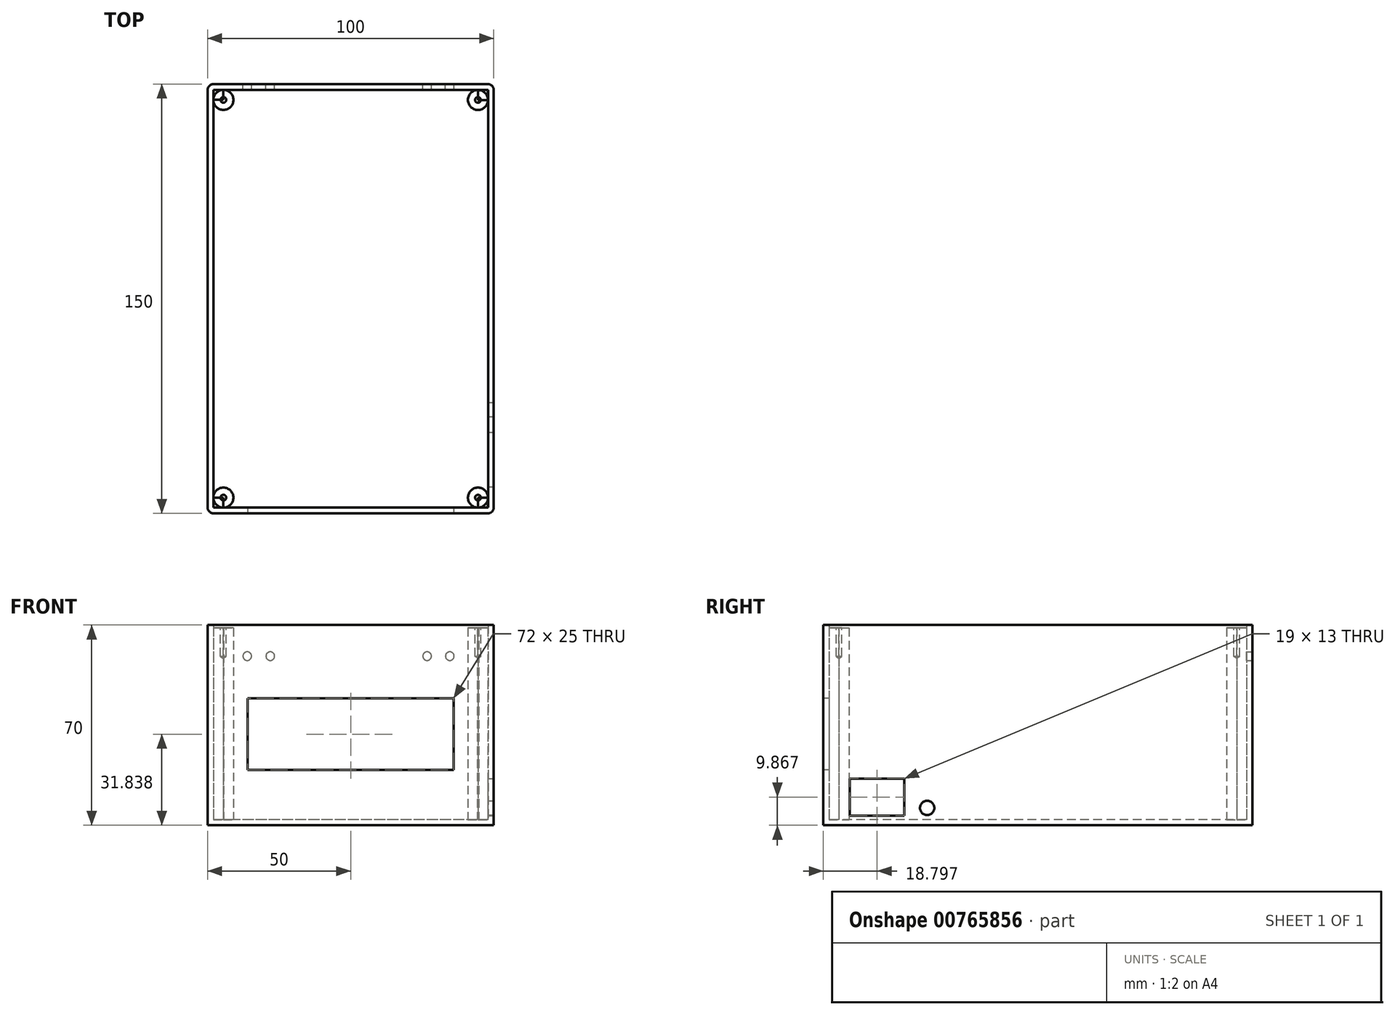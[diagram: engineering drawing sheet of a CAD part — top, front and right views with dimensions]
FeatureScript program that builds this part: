
annotation { "Feature Type Name" : "Feature", "Feature Type Description" : "" }
export const myFeature = defineFeature(function(context is Context, id is Id, definition is map)
    precondition{}
    {
        {
            var Q0;
            Q0=qCreatedBy(makeId("Top.planeOp"),FACE);
            var sketch = newSketch(context, id + "F0", { "sketchPlane" : qUnion([Q0])});
            skLineSegment(sketch, "E0.bottom", {"start": v(50, 75) * mm, "end": v(-50, 75) * mm});
            skLineSegment(sketch, "E0.top", {"start": v(50, -75) * mm, "end": v(-50, -75) * mm});
            skLineSegment(sketch, "E0.left", {"start": v(50, 75) * mm, "end": v(50, -75) * mm});
            skLineSegment(sketch, "E0.right", {"start": v(-50, 75) * mm, "end": v(-50, -75) * mm});
            skPoint(sketch, "E0.middle", {"position": v(0, 0) * mm});
            skSolve(sketch);
        }
        {
            var Q0;
            Q0=qSketchRegion(id+"F0",true);
            extrude(context, id + "F1", {"entities" : qUnion([Q0]), "depth" : 70 * mm, "offsetDistance" : 25.4 * mm});
        }
        {
            var Q0;
            Q0=makeQuery(id+"F1.opExtrude","CAP_FACE",FACE,{"disambiguationData":[OSD([sQuery(id+"F0.wireOp",EDGE,"E0.bottom"),sQuery(id+"F0.wireOp",EDGE,"E0.top"),sQuery(id+"F0.wireOp",EDGE,"E0.left"),sQuery(id+"F0.wireOp",EDGE,"E0.right")])],"isStart":false});
            shell(context, id + "F2", {"entities" : qUnion([Q0]), "thickness" : 2 * mm});
        }
        {
            var Q0;
            Q0=makeQuery(id+"F1.opExtrude","SWEPT_FACE",FACE,{"disambiguationData":[OSD([sQuery(id+"F0.wireOp",EDGE,"E0.top")])]});
            var sketch = newSketch(context, id + "F3", { "sketchPlane" : qUnion([Q0])});
            skLineSegment(sketch, "E1.bottom", {"start": v(-36, 44.34) * mm, "end": v(36, 44.34) * mm});
            skLineSegment(sketch, "E1.top", {"start": v(-36, 19.34) * mm, "end": v(36, 19.34) * mm});
            skLineSegment(sketch, "E1.left", {"start": v(-36, 44.34) * mm, "end": v(-36, 19.34) * mm});
            skLineSegment(sketch, "E1.right", {"start": v(36, 44.34) * mm, "end": v(36, 19.34) * mm});
            skPoint(sketch, "E1.middle", {"position": v(0, 31.84) * mm});
            skSolve(sketch);
        }
        {
            var Q0;
            Q0=qSketchRegion(id+"F3",true);
            extrude(context, id + "F4", {"entities" : qUnion([Q0]), "operationType" : NewBodyOperationType.REMOVE, "oppositeDirection" : true, "depth" : 3 * mm, "offsetDistance" : 25.4 * mm});
        }
        {
            var Q0;
            Q0=makeQuery(id+"F1.opExtrude","SWEPT_FACE",FACE,{"disambiguationData":[OSD([sQuery(id+"F0.wireOp",EDGE,"E0.bottom")])]});
            var sketch = newSketch(context, id + "F5", { "sketchPlane" : qUnion([Q0])});
            skPoint(sketch, "E2", {"position": v(-34.63, 59.1) * mm});
            skPoint(sketch, "E3", {"position": v(-26.71, 59.1) * mm});
            skPoint(sketch, "E4", {"position": v(36.15, 59.1) * mm});
            skPoint(sketch, "E5", {"position": v(28.12, 59.1) * mm});
            skSolve(sketch);
        }
        {
            var Q0;
            Q0=sQuery(id+"F5.wireOp",VERTEX,"E2");
            var Q1;
            Q1=sQuery(id+"F5.wireOp",VERTEX,"E3");
            var Q2;
            Q2=sQuery(id+"F5.wireOp",VERTEX,"E5");
            var Q3;
            Q3=sQuery(id+"F5.wireOp",VERTEX,"E4");
            var Q4;
            Q4=makeQuery(id+"F1.opExtrude","SWEPT_BODY",BODY,{"disambiguationData":[OSD([sQuery(id+"F0.wireOp",EDGE,"E0.bottom"),sQuery(id+"F0.wireOp",EDGE,"E0.top"),sQuery(id+"F0.wireOp",EDGE,"E0.left"),sQuery(id+"F0.wireOp",EDGE,"E0.right")])]});
            hole(context, id + "F6", {"style" : HoleStyle.SIMPLE, "endStyle" : HoleEndStyle.BLIND, "holeDiameter" : 3 * mm, "majorDiameter" : 6.35 * mm, "holeDepth" : 4 * mm, "isTappedThrough" : true, "tappedDepth" : 12.7 * mm, "tapClearance" : 3, "startFromSketch" : true, "locations" : qUnion([Q0, Q1, Q2, Q3]), "scope" : qUnion([Q4])});
        }
        {
            var Q0;
            Q0=makeQuery(id+"F1.opExtrude","SWEPT_FACE",FACE,{"disambiguationData":[OSD([sQuery(id+"F0.wireOp",EDGE,"E0.left")])]});
            var sketch = newSketch(context, id + "F7", { "sketchPlane" : qUnion([Q0])});
            skPoint(sketch, "E6", {"position": v(-38.7, 6.06) * mm});
            skSolve(sketch);
        }
        {
            var Q0;
            Q0=sQuery(id+"F7.wireOp",VERTEX,"E6");
            var Q1;
            Q1=makeQuery(id+"F1.opExtrude","SWEPT_BODY",BODY,{"disambiguationData":[OSD([sQuery(id+"F0.wireOp",EDGE,"E0.bottom"),sQuery(id+"F0.wireOp",EDGE,"E0.top"),sQuery(id+"F0.wireOp",EDGE,"E0.left"),sQuery(id+"F0.wireOp",EDGE,"E0.right")])]});
            hole(context, id + "F8", {"style" : HoleStyle.SIMPLE, "endStyle" : HoleEndStyle.BLIND, "holeDiameter" : 5 * mm, "majorDiameter" : 6.35 * mm, "holeDepth" : 4 * mm, "isTappedThrough" : true, "tappedDepth" : 12.7 * mm, "tapClearance" : 3, "startFromSketch" : true, "locations" : qUnion([Q0]), "scope" : qUnion([Q1])});
        }
        {
            var Q0;
            Q0=makeQuery(id+"F1.opExtrude","SWEPT_EDGE",EDGE,{"disambiguationData":[OSD([sQuery(id+"F0.wireOp",EDGE,"E0.top"),sQuery(id+"F0.wireOp",EDGE,"E0.right")])]});
            var Q1;
            Q1=makeQuery(id+"F1.opExtrude","SWEPT_EDGE",EDGE,{"disambiguationData":[OSD([sQuery(id+"F0.wireOp",EDGE,"E0.bottom"),sQuery(id+"F0.wireOp",EDGE,"E0.right")])]});
            var Q2;
            Q2=makeQuery(id+"F1.opExtrude","SWEPT_EDGE",EDGE,{"disambiguationData":[OSD([sQuery(id+"F0.wireOp",EDGE,"E0.bottom"),sQuery(id+"F0.wireOp",EDGE,"E0.left")])]});
            var Q3;
            Q3=makeQuery(id+"F1.opExtrude","SWEPT_EDGE",EDGE,{"disambiguationData":[OSD([sQuery(id+"F0.wireOp",EDGE,"E0.top"),sQuery(id+"F0.wireOp",EDGE,"E0.left")])]});
            fillet(context, id + "F9", {"entities" : qUnion([Q0, Q1, Q2, Q3]), "radius" : 2 * mm, "tangentPropagation" : true, "allowEdgeOverflow" : false});
        }
        {
            var Q0;
            Q0=makeQuery(id+"F2.opShell","OFFSET_FACE",FACE,{"disambiguationData":[OSD([sQuery(id+"F0.wireOp",EDGE,"E0.bottom"),sQuery(id+"F0.wireOp",EDGE,"E0.top"),sQuery(id+"F0.wireOp",EDGE,"E0.left"),sQuery(id+"F0.wireOp",EDGE,"E0.right")])]});
            var sketch = newSketch(context, id + "F10", { "sketchPlane" : qUnion([Q0])});
            skCircle(sketch, "E7", {"center": v(-44.5, 69.5) * mm, "radius": 3.5 * mm});
            skSolve(sketch);
        }
        {
            var Q0;
            Q0=makeQuery(id+"F10.imprint","IMPRINT",FACE,{"disambiguationData":[TD([[makeQuery(id+"F10.imprint","IMPRINT",EDGE,{"derivedFrom":sQuery(id+"F10.wireOp",EDGE,"E7")}),-1.0]])]});
            var sketch = newSketch(context, id + "F11", { "sketchPlane" : qUnion([Q0])});
            skCircle(sketch, "E8", {"center": v(44.49, 69.47) * mm, "radius": 3.5 * mm});
            skSolve(sketch);
        }
        {
            var Q0;
            Q0=makeQuery(id+"F10.imprint","IMPRINT",FACE,{"disambiguationData":[TD([[makeQuery(id+"F10.imprint","IMPRINT",EDGE,{"derivedFrom":sQuery(id+"F10.wireOp",EDGE,"E7")}),-1.0]])]});
            var sketch = newSketch(context, id + "F12", { "sketchPlane" : qUnion([Q0])});
            skCircle(sketch, "E9", {"center": v(44.5, -69.5) * mm, "radius": 3.5 * mm});
            skSolve(sketch);
        }
        {
            var Q0;
            Q0=makeQuery(id+"F10.imprint","IMPRINT",FACE,{"disambiguationData":[TD([[makeQuery(id+"F10.imprint","IMPRINT",EDGE,{"derivedFrom":sQuery(id+"F10.wireOp",EDGE,"E7")}),-1.0]])]});
            var sketch = newSketch(context, id + "F13", { "sketchPlane" : qUnion([Q0])});
            skCircle(sketch, "E10", {"center": v(-44.5, -69.5) * mm, "radius": 3.5 * mm});
            skSolve(sketch);
        }
        {
            var Q0;
            Q0=qSketchRegion(id+"F10",true);
            var Q1;
            Q1=qSketchRegion(id+"F11",true);
            var Q2;
            Q2=qSketchRegion(id+"F13",true);
            var Q3;
            Q3=qSketchRegion(id+"F12",true);
            extrude(context, id + "F14", {"entities" : qUnion([Q0, Q1, Q2, Q3]), "operationType" : NewBodyOperationType.ADD, "depth" : 67 * mm, "offsetDistance" : 25.4 * mm});
        }
        {
            var Q0;
            Q0=makeQuery(id+"F2.opShell","OFFSET_FACE",FACE,{"disambiguationData":[OSD([sQuery(id+"F0.wireOp",EDGE,"E0.bottom"),sQuery(id+"F0.wireOp",EDGE,"E0.top"),sQuery(id+"F0.wireOp",EDGE,"E0.left"),sQuery(id+"F0.wireOp",EDGE,"E0.right")])]});
            var sketch = newSketch(context, id + "F15", { "sketchPlane" : qUnion([Q0])});
            skLineSegment(sketch, "E11.bottom", {"start": v(-44.5, 69.5) * mm, "end": v(-48, 69.5) * mm});
            skLineSegment(sketch, "E11.top", {"start": v(-44.5, 73) * mm, "end": v(-48, 73) * mm});
            skLineSegment(sketch, "E11.left", {"start": v(-44.5, 69.5) * mm, "end": v(-44.5, 73) * mm});
            skLineSegment(sketch, "E11.right", {"start": v(-48, 69.5) * mm, "end": v(-48, 73) * mm});
            skLineSegment(sketch, "E12.bottom", {"start": v(44.49, 69.47) * mm, "end": v(47.99, 69.47) * mm});
            skLineSegment(sketch, "E12.top", {"start": v(44.49, 72.97) * mm, "end": v(47.99, 72.97) * mm});
            skLineSegment(sketch, "E12.left", {"start": v(44.49, 69.47) * mm, "end": v(44.49, 72.97) * mm});
            skLineSegment(sketch, "E12.right", {"start": v(47.99, 69.47) * mm, "end": v(47.99, 72.97) * mm});
            skLineSegment(sketch, "E13.bottom", {"start": v(44.5, -69.5) * mm, "end": v(48, -69.5) * mm});
            skLineSegment(sketch, "E13.top", {"start": v(44.5, -73) * mm, "end": v(48, -73) * mm});
            skLineSegment(sketch, "E13.left", {"start": v(44.5, -69.5) * mm, "end": v(44.5, -73) * mm});
            skLineSegment(sketch, "E13.right", {"start": v(48, -69.5) * mm, "end": v(48, -73) * mm});
            skLineSegment(sketch, "E14.bottom", {"start": v(-44.5, -69.5) * mm, "end": v(-48, -69.5) * mm});
            skLineSegment(sketch, "E14.top", {"start": v(-44.5, -73) * mm, "end": v(-48, -73) * mm});
            skLineSegment(sketch, "E14.left", {"start": v(-44.5, -69.5) * mm, "end": v(-44.5, -73) * mm});
            skLineSegment(sketch, "E14.right", {"start": v(-48, -69.5) * mm, "end": v(-48, -73) * mm});
            skSolve(sketch);
        }
        {
            var Q0;
            Q0=qSketchRegion(id+"F15",true);
            extrude(context, id + "F16", {"entities" : qUnion([Q0]), "depth" : 67 * mm, "offsetDistance" : 25.4 * mm});
        }
        {
            var Q0;
            Q0=makeQuery(id+"F14.opExtrude","CAP_FACE",FACE,{"disambiguationData":[OSD([sQuery(id+"F10.wireOp",EDGE,"E7")])],"isStart":false});
            var sketch = newSketch(context, id + "F17", { "sketchPlane" : qUnion([Q0])});
            skPoint(sketch, "E15", {"position": v(-44.5, -69.5) * mm});
            skSolve(sketch);
        }
        {
            var Q0;
            Q0=makeQuery(id+"F16.opExtrude","CAP_FACE",FACE,{"disambiguationData":[OSD([sQuery(id+"F15.wireOp",EDGE,"E11.bottom"),sQuery(id+"F15.wireOp",EDGE,"E11.top"),sQuery(id+"F15.wireOp",EDGE,"E11.left"),sQuery(id+"F15.wireOp",EDGE,"E11.right")])],"isStart":false});
            var sketch = newSketch(context, id + "F18", { "sketchPlane" : qUnion([Q0])});
            skPoint(sketch, "E16", {"position": v(-44.5, 69.5) * mm});
            skSolve(sketch);
        }
        {
            var Q0;
            Q0=makeQuery(id+"F16.opExtrude","CAP_FACE",FACE,{"disambiguationData":[OSD([sQuery(id+"F15.wireOp",EDGE,"E12.bottom"),sQuery(id+"F15.wireOp",EDGE,"E12.top"),sQuery(id+"F15.wireOp",EDGE,"E12.left"),sQuery(id+"F15.wireOp",EDGE,"E12.right")])],"isStart":false});
            var sketch = newSketch(context, id + "F19", { "sketchPlane" : qUnion([Q0])});
            skPoint(sketch, "E17", {"position": v(44.49, 69.47) * mm});
            skSolve(sketch);
        }
        {
            var Q0;
            Q0=makeQuery(id+"F16.opExtrude","CAP_FACE",FACE,{"disambiguationData":[OSD([sQuery(id+"F15.wireOp",EDGE,"E13.bottom"),sQuery(id+"F15.wireOp",EDGE,"E13.top"),sQuery(id+"F15.wireOp",EDGE,"E13.left"),sQuery(id+"F15.wireOp",EDGE,"E13.right")])],"isStart":false});
            var sketch = newSketch(context, id + "F20", { "sketchPlane" : qUnion([Q0])});
            skPoint(sketch, "E18", {"position": v(44.5, -69.5) * mm});
            skSolve(sketch);
        }
        {
            var Q0;
            Q0=sQuery(id+"F17.wireOp",VERTEX,"E15");
            var Q1;
            Q1=sQuery(id+"F18.wireOp",VERTEX,"E16");
            var Q2;
            Q2=sQuery(id+"F19.wireOp",VERTEX,"E17");
            var Q3;
            Q3=sQuery(id+"F20.wireOp",VERTEX,"E18");
            var Q4;
            Q4=makeQuery(id+"F1.opExtrude","SWEPT_BODY",BODY,{"disambiguationData":[OSD([sQuery(id+"F0.wireOp",EDGE,"E0.bottom"),sQuery(id+"F0.wireOp",EDGE,"E0.top"),sQuery(id+"F0.wireOp",EDGE,"E0.left"),sQuery(id+"F0.wireOp",EDGE,"E0.right")])]});
            var Q5;
            Q5=makeQuery(id+"F16.opExtrude","SWEPT_BODY",BODY,{"disambiguationData":[OSD([sQuery(id+"F15.wireOp",EDGE,"E14.bottom"),sQuery(id+"F15.wireOp",EDGE,"E14.top"),sQuery(id+"F15.wireOp",EDGE,"E14.left"),sQuery(id+"F15.wireOp",EDGE,"E14.right")])]});
            var Q6;
            Q6=makeQuery(id+"F16.opExtrude","SWEPT_BODY",BODY,{"disambiguationData":[OSD([sQuery(id+"F15.wireOp",EDGE,"E11.bottom"),sQuery(id+"F15.wireOp",EDGE,"E11.top"),sQuery(id+"F15.wireOp",EDGE,"E11.left"),sQuery(id+"F15.wireOp",EDGE,"E11.right")])]});
            var Q7;
            Q7=makeQuery(id+"F16.opExtrude","SWEPT_BODY",BODY,{"disambiguationData":[OSD([sQuery(id+"F15.wireOp",EDGE,"E12.bottom"),sQuery(id+"F15.wireOp",EDGE,"E12.top"),sQuery(id+"F15.wireOp",EDGE,"E12.left"),sQuery(id+"F15.wireOp",EDGE,"E12.right")])]});
            var Q8;
            Q8=makeQuery(id+"F16.opExtrude","SWEPT_BODY",BODY,{"disambiguationData":[OSD([sQuery(id+"F15.wireOp",EDGE,"E13.bottom"),sQuery(id+"F15.wireOp",EDGE,"E13.top"),sQuery(id+"F15.wireOp",EDGE,"E13.left"),sQuery(id+"F15.wireOp",EDGE,"E13.right")])]});
            hole(context, id + "F21", {"style" : HoleStyle.SIMPLE, "endStyle" : HoleEndStyle.BLIND, "holeDiameter" : 2 * mm, "majorDiameter" : 6.35 * mm, "holeDepth" : 10 * mm, "isTappedThrough" : true, "tappedDepth" : 12.7 * mm, "tapClearance" : 3, "startFromSketch" : true, "locations" : qUnion([Q0, Q1, Q2, Q3]), "scope" : qUnion([Q4, Q5, Q6, Q7, Q8])});
        }
        {
            var Q0;
            Q0=makeQuery(id+"F1.opExtrude","SWEPT_FACE",FACE,{"disambiguationData":[OSD([sQuery(id+"F0.wireOp",EDGE,"E0.left")])]});
            var sketch = newSketch(context, id + "F22", { "sketchPlane" : qUnion([Q0])});
            skLineSegment(sketch, "E19.bottom", {"start": v(-65.7, 3.37) * mm, "end": v(-46.7, 3.37) * mm});
            skLineSegment(sketch, "E19.top", {"start": v(-65.7, 16.37) * mm, "end": v(-46.7, 16.37) * mm});
            skLineSegment(sketch, "E19.left", {"start": v(-65.7, 3.37) * mm, "end": v(-65.7, 16.37) * mm});
            skLineSegment(sketch, "E19.right", {"start": v(-46.7, 3.37) * mm, "end": v(-46.7, 16.37) * mm});
            skPoint(sketch, "E19.middle", {"position": v(-54.68, 16.22) * mm});
            skSolve(sketch);
        }
        {
            var Q0;
            Q0=qSketchRegion(id+"F22",true);
            extrude(context, id + "F23", {"entities" : qUnion([Q0]), "operationType" : NewBodyOperationType.REMOVE, "oppositeDirection" : true, "depth" : 25.4 * mm, "offsetDistance" : 25.4 * mm});
        }
    });
